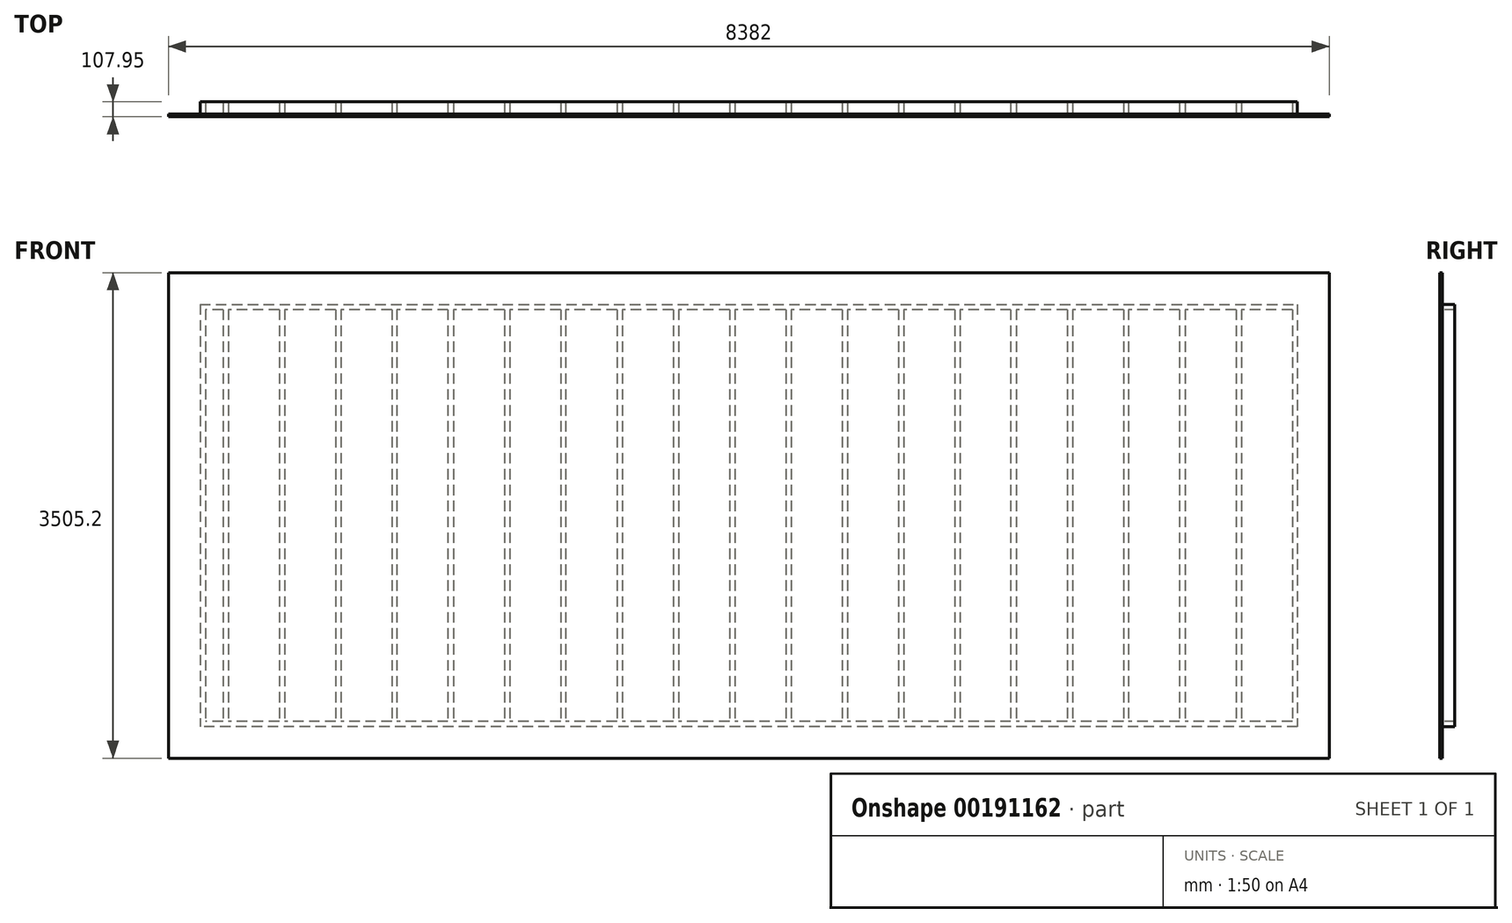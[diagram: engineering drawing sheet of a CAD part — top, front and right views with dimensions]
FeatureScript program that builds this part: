
annotation { "Feature Type Name" : "Feature", "Feature Type Description" : "" }
export const myFeature = defineFeature(function(context is Context, id is Id, definition is map)
    precondition{}
    {
        {
            var Q0;
            Q0=qCreatedBy(makeId("Top.planeOp"),FACE);
            var sketch = newSketch(context, id + "F0", { "sketchPlane" : qUnion([Q0])});
            skLineSegment(sketch, "E0.bottom", {"start": v(3962.4, -44.45) * mm, "end": v(-3962.4, -44.45) * mm});
            skLineSegment(sketch, "E0.top", {"start": v(3962.4, 44.45) * mm, "end": v(-3962.4, 44.45) * mm});
            skLineSegment(sketch, "E0.left", {"start": v(3962.4, -44.45) * mm, "end": v(3962.4, 44.45) * mm});
            skLineSegment(sketch, "E0.right", {"start": v(-3962.4, -44.45) * mm, "end": v(-3962.4, 44.45) * mm});
            skPoint(sketch, "E0.middle", {"position": v(0, 0) * mm});
            skSolve(sketch);
        }
        {
            var Q0;
            Q0 = qSketchRegion(id + "F0", true);
            extrude(context, id + "F1", {"entities" : qUnion([Q0]), "depth" : 38.1 * mm});
        }
        {
            var Q0;
            Q0=makeQuery(id+"F1.opExtrude","CAP_FACE",FACE,{"disambiguationData":[OSD([sQuery(id+"F0.wireOp",EDGE,"E0.bottom"),sQuery(id+"F0.wireOp",EDGE,"E0.top"),sQuery(id+"F0.wireOp",EDGE,"E0.left"),sQuery(id+"F0.wireOp",EDGE,"E0.right")])],"isStart":false});
            var sketch = newSketch(context, id + "F2", { "sketchPlane" : qUnion([Q0])});
            skLineSegment(sketch, "E1.bottom", {"start": v(3962.4, 44.45) * mm, "end": v(3924.3, 44.45) * mm});
            skLineSegment(sketch, "E1.top", {"start": v(3962.4, -44.45) * mm, "end": v(3924.3, -44.45) * mm});
            skLineSegment(sketch, "E1.left", {"start": v(3962.4, 44.45) * mm, "end": v(3962.4, -44.45) * mm});
            skLineSegment(sketch, "E1.right", {"start": v(3924.3, 44.45) * mm, "end": v(3924.3, -44.45) * mm});
            skLineSegment(sketch, "E2.bottom", {"start": v(3556, 44.45) * mm, "end": v(3517.9, 44.45) * mm});
            skLineSegment(sketch, "E2.top", {"start": v(3556, -44.45) * mm, "end": v(3517.9, -44.45) * mm});
            skLineSegment(sketch, "E2.left", {"start": v(3556, 44.45) * mm, "end": v(3556, -44.45) * mm});
            skLineSegment(sketch, "E2.right", {"start": v(3517.9, 44.45) * mm, "end": v(3517.9, -44.45) * mm});
            skLineSegment(sketch, "E3.bottom", {"start": v(3149.6, 44.45) * mm, "end": v(3111.5, 44.45) * mm});
            skLineSegment(sketch, "E3.top", {"start": v(3149.6, -44.45) * mm, "end": v(3111.5, -44.45) * mm});
            skLineSegment(sketch, "E3.left", {"start": v(3149.6, 44.45) * mm, "end": v(3149.6, -44.45) * mm});
            skLineSegment(sketch, "E3.right", {"start": v(3111.5, 44.45) * mm, "end": v(3111.5, -44.45) * mm});
            skLineSegment(sketch, "E4.bottom", {"start": v(2705.1, 44.45) * mm, "end": v(2743.2, 44.45) * mm});
            skLineSegment(sketch, "E4.top", {"start": v(2705.1, -44.45) * mm, "end": v(2743.2, -44.45) * mm});
            skLineSegment(sketch, "E4.left", {"start": v(2705.1, 44.45) * mm, "end": v(2705.1, -44.45) * mm});
            skLineSegment(sketch, "E4.right", {"start": v(2743.2, 44.45) * mm, "end": v(2743.2, -44.45) * mm});
            skLineSegment(sketch, "E5.bottom", {"start": v(2336.8, 44.45) * mm, "end": v(2298.7, 44.45) * mm});
            skLineSegment(sketch, "E5.top", {"start": v(2336.8, -44.45) * mm, "end": v(2298.7, -44.45) * mm});
            skLineSegment(sketch, "E5.left", {"start": v(2336.8, 44.45) * mm, "end": v(2336.8, -44.45) * mm});
            skLineSegment(sketch, "E5.right", {"start": v(2298.7, 44.45) * mm, "end": v(2298.7, -44.45) * mm});
            skLineSegment(sketch, "E6.bottom", {"start": v(1930.4, 44.45) * mm, "end": v(1892.3, 44.45) * mm});
            skLineSegment(sketch, "E6.top", {"start": v(1930.4, -44.45) * mm, "end": v(1892.3, -44.45) * mm});
            skLineSegment(sketch, "E6.left", {"start": v(1930.4, 44.45) * mm, "end": v(1930.4, -44.45) * mm});
            skLineSegment(sketch, "E6.right", {"start": v(1892.3, 44.45) * mm, "end": v(1892.3, -44.45) * mm});
            skLineSegment(sketch, "E7.bottom", {"start": v(1524, 44.45) * mm, "end": v(1485.9, 44.45) * mm});
            skLineSegment(sketch, "E7.top", {"start": v(1524, -44.45) * mm, "end": v(1485.9, -44.45) * mm});
            skLineSegment(sketch, "E7.left", {"start": v(1524, 44.45) * mm, "end": v(1524, -44.45) * mm});
            skLineSegment(sketch, "E7.right", {"start": v(1485.9, 44.45) * mm, "end": v(1485.9, -44.45) * mm});
            skLineSegment(sketch, "E8.bottom", {"start": v(1117.6, 44.45) * mm, "end": v(1079.5, 44.45) * mm});
            skLineSegment(sketch, "E8.top", {"start": v(1117.6, -44.45) * mm, "end": v(1079.5, -44.45) * mm});
            skLineSegment(sketch, "E8.left", {"start": v(1117.6, 44.45) * mm, "end": v(1117.6, -44.45) * mm});
            skLineSegment(sketch, "E8.right", {"start": v(1079.5, 44.45) * mm, "end": v(1079.5, -44.45) * mm});
            skLineSegment(sketch, "E9.bottom", {"start": v(711.2, 44.45) * mm, "end": v(673.1, 44.45) * mm});
            skLineSegment(sketch, "E9.top", {"start": v(711.2, -44.45) * mm, "end": v(673.1, -44.45) * mm});
            skLineSegment(sketch, "E9.left", {"start": v(711.2, 44.45) * mm, "end": v(711.2, -44.45) * mm});
            skLineSegment(sketch, "E9.right", {"start": v(673.1, 44.45) * mm, "end": v(673.1, -44.45) * mm});
            skLineSegment(sketch, "E10.bottom", {"start": v(304.8, 44.45) * mm, "end": v(266.7, 44.45) * mm});
            skLineSegment(sketch, "E10.top", {"start": v(304.8, -44.45) * mm, "end": v(266.7, -44.45) * mm});
            skLineSegment(sketch, "E10.left", {"start": v(304.8, 44.45) * mm, "end": v(304.8, -44.45) * mm});
            skLineSegment(sketch, "E10.right", {"start": v(266.7, 44.45) * mm, "end": v(266.7, -44.45) * mm});
            skLineSegment(sketch, "E11.bottom", {"start": v(-101.6, 44.45) * mm, "end": v(-139.7, 44.45) * mm});
            skLineSegment(sketch, "E11.top", {"start": v(-101.6, -44.45) * mm, "end": v(-139.7, -44.45) * mm});
            skLineSegment(sketch, "E11.left", {"start": v(-101.6, 44.45) * mm, "end": v(-101.6, -44.45) * mm});
            skLineSegment(sketch, "E11.right", {"start": v(-139.7, 44.45) * mm, "end": v(-139.7, -44.45) * mm});
            skLineSegment(sketch, "E12.bottom", {"start": v(-508, 44.45) * mm, "end": v(-546.1, 44.45) * mm});
            skLineSegment(sketch, "E12.top", {"start": v(-508, -44.45) * mm, "end": v(-546.1, -44.45) * mm});
            skLineSegment(sketch, "E12.left", {"start": v(-508, 44.45) * mm, "end": v(-508, -44.45) * mm});
            skLineSegment(sketch, "E12.right", {"start": v(-546.1, 44.45) * mm, "end": v(-546.1, -44.45) * mm});
            skLineSegment(sketch, "E13.bottom", {"start": v(-914.4, 44.45) * mm, "end": v(-952.5, 44.45) * mm});
            skLineSegment(sketch, "E13.top", {"start": v(-914.4, -44.45) * mm, "end": v(-952.5, -44.45) * mm});
            skLineSegment(sketch, "E13.left", {"start": v(-914.4, 44.45) * mm, "end": v(-914.4, -44.45) * mm});
            skLineSegment(sketch, "E13.right", {"start": v(-952.5, 44.45) * mm, "end": v(-952.5, -44.45) * mm});
            skLineSegment(sketch, "E14.bottom", {"start": v(-1320.8, 44.45) * mm, "end": v(-1358.9, 44.45) * mm});
            skLineSegment(sketch, "E14.top", {"start": v(-1320.8, -44.45) * mm, "end": v(-1358.9, -44.45) * mm});
            skLineSegment(sketch, "E14.left", {"start": v(-1320.8, 44.45) * mm, "end": v(-1320.8, -44.45) * mm});
            skLineSegment(sketch, "E14.right", {"start": v(-1358.9, 44.45) * mm, "end": v(-1358.9, -44.45) * mm});
            skLineSegment(sketch, "E15.bottom", {"start": v(-1727.2, 44.45) * mm, "end": v(-1765.3, 44.45) * mm});
            skLineSegment(sketch, "E15.top", {"start": v(-1727.2, -44.45) * mm, "end": v(-1765.3, -44.45) * mm});
            skLineSegment(sketch, "E15.left", {"start": v(-1727.2, 44.45) * mm, "end": v(-1727.2, -44.45) * mm});
            skLineSegment(sketch, "E15.right", {"start": v(-1765.3, 44.45) * mm, "end": v(-1765.3, -44.45) * mm});
            skLineSegment(sketch, "E16.bottom", {"start": v(-2133.6, 44.45) * mm, "end": v(-2171.7, 44.45) * mm});
            skLineSegment(sketch, "E16.top", {"start": v(-2133.6, -44.45) * mm, "end": v(-2171.7, -44.45) * mm});
            skLineSegment(sketch, "E16.left", {"start": v(-2133.6, 44.45) * mm, "end": v(-2133.6, -44.45) * mm});
            skLineSegment(sketch, "E16.right", {"start": v(-2171.7, 44.45) * mm, "end": v(-2171.7, -44.45) * mm});
            skLineSegment(sketch, "E17.bottom", {"start": v(-2540, 44.45) * mm, "end": v(-2578.1, 44.45) * mm});
            skLineSegment(sketch, "E17.top", {"start": v(-2540, -44.45) * mm, "end": v(-2578.1, -44.45) * mm});
            skLineSegment(sketch, "E17.left", {"start": v(-2540, 44.45) * mm, "end": v(-2540, -44.45) * mm});
            skLineSegment(sketch, "E17.right", {"start": v(-2578.1, 44.45) * mm, "end": v(-2578.1, -44.45) * mm});
            skLineSegment(sketch, "E18.bottom", {"start": v(-2946.4, 44.45) * mm, "end": v(-2984.5, 44.45) * mm});
            skLineSegment(sketch, "E18.top", {"start": v(-2946.4, -44.45) * mm, "end": v(-2984.5, -44.45) * mm});
            skLineSegment(sketch, "E18.left", {"start": v(-2946.4, 44.45) * mm, "end": v(-2946.4, -44.45) * mm});
            skLineSegment(sketch, "E18.right", {"start": v(-2984.5, 44.45) * mm, "end": v(-2984.5, -44.45) * mm});
            skLineSegment(sketch, "E19.bottom", {"start": v(-3962.4, 44.45) * mm, "end": v(-3924.3, 44.45) * mm});
            skLineSegment(sketch, "E19.top", {"start": v(-3962.4, -44.45) * mm, "end": v(-3924.3, -44.45) * mm});
            skLineSegment(sketch, "E19.left", {"start": v(-3962.4, 44.45) * mm, "end": v(-3962.4, -44.45) * mm});
            skLineSegment(sketch, "E19.right", {"start": v(-3924.3, 44.45) * mm, "end": v(-3924.3, -44.45) * mm});
            skLineSegment(sketch, "E20.bottom", {"start": v(-3390.9, 44.45) * mm, "end": v(-3352.8, 44.45) * mm});
            skLineSegment(sketch, "E20.top", {"start": v(-3390.9, -44.45) * mm, "end": v(-3352.8, -44.45) * mm});
            skLineSegment(sketch, "E20.left", {"start": v(-3390.9, 44.45) * mm, "end": v(-3390.9, -44.45) * mm});
            skLineSegment(sketch, "E20.right", {"start": v(-3352.8, 44.45) * mm, "end": v(-3352.8, -44.45) * mm});
            skLineSegment(sketch, "E21.bottom", {"start": v(-3797.3, 44.45) * mm, "end": v(-3759.2, 44.45) * mm});
            skLineSegment(sketch, "E21.top", {"start": v(-3797.3, -44.45) * mm, "end": v(-3759.2, -44.45) * mm});
            skLineSegment(sketch, "E21.left", {"start": v(-3797.3, 44.45) * mm, "end": v(-3797.3, -44.45) * mm});
            skLineSegment(sketch, "E21.right", {"start": v(-3759.2, 44.45) * mm, "end": v(-3759.2, -44.45) * mm});
            skSolve(sketch);
        }
        {
            var Q0;
            Q0 = qSketchRegion(id + "F2", true);
            extrude(context, id + "F3", {"entities" : qUnion([Q0]), "operationType" : NewBodyOperationType.ADD, "depth" : 2971.8 * mm});
        }
        {
            var Q0;
            Q0=makeQuery(id+"F3.boolean.opBoolean","MERGE",FACE,{"derivedFrom":[makeQuery(id+"F1.opExtrude","SWEPT_FACE",FACE,{"disambiguationData":[OSD([sQuery(id+"F0.wireOp",EDGE,"E0.bottom")])]}),makeQuery(id+"F3.opExtrude","SWEPT_FACE",FACE,{"disambiguationData":[OSD([sQuery(id+"F2.wireOp",EDGE,"E1.top")])]}),makeQuery(id+"F3.opExtrude","SWEPT_FACE",FACE,{"disambiguationData":[OSD([sQuery(id+"F2.wireOp",EDGE,"E2.top")])]}),makeQuery(id+"F3.opExtrude","SWEPT_FACE",FACE,{"disambiguationData":[OSD([sQuery(id+"F2.wireOp",EDGE,"E3.top")])]}),makeQuery(id+"F3.opExtrude","SWEPT_FACE",FACE,{"disambiguationData":[OSD([sQuery(id+"F2.wireOp",EDGE,"E4.top")])]}),makeQuery(id+"F3.opExtrude","SWEPT_FACE",FACE,{"disambiguationData":[OSD([sQuery(id+"F2.wireOp",EDGE,"E5.top")])]}),makeQuery(id+"F3.opExtrude","SWEPT_FACE",FACE,{"disambiguationData":[OSD([sQuery(id+"F2.wireOp",EDGE,"E6.top")])]}),makeQuery(id+"F3.opExtrude","SWEPT_FACE",FACE,{"disambiguationData":[OSD([sQuery(id+"F2.wireOp",EDGE,"E7.top")])]}),makeQuery(id+"F3.opExtrude","SWEPT_FACE",FACE,{"disambiguationData":[OSD([sQuery(id+"F2.wireOp",EDGE,"E8.top")])]}),makeQuery(id+"F3.opExtrude","SWEPT_FACE",FACE,{"disambiguationData":[OSD([sQuery(id+"F2.wireOp",EDGE,"E9.top")])]}),makeQuery(id+"F3.opExtrude","SWEPT_FACE",FACE,{"disambiguationData":[OSD([sQuery(id+"F2.wireOp",EDGE,"E10.top")])]}),makeQuery(id+"F3.opExtrude","SWEPT_FACE",FACE,{"disambiguationData":[OSD([sQuery(id+"F2.wireOp",EDGE,"E11.top")])]}),makeQuery(id+"F3.opExtrude","SWEPT_FACE",FACE,{"disambiguationData":[OSD([sQuery(id+"F2.wireOp",EDGE,"E12.top")])]}),makeQuery(id+"F3.opExtrude","SWEPT_FACE",FACE,{"disambiguationData":[OSD([sQuery(id+"F2.wireOp",EDGE,"E13.top")])]}),makeQuery(id+"F3.opExtrude","SWEPT_FACE",FACE,{"disambiguationData":[OSD([sQuery(id+"F2.wireOp",EDGE,"E14.top")])]}),makeQuery(id+"F3.opExtrude","SWEPT_FACE",FACE,{"disambiguationData":[OSD([sQuery(id+"F2.wireOp",EDGE,"E15.top")])]}),makeQuery(id+"F3.opExtrude","SWEPT_FACE",FACE,{"disambiguationData":[OSD([sQuery(id+"F2.wireOp",EDGE,"E16.top")])]}),makeQuery(id+"F3.opExtrude","SWEPT_FACE",FACE,{"disambiguationData":[OSD([sQuery(id+"F2.wireOp",EDGE,"E17.top")])]}),makeQuery(id+"F3.opExtrude","SWEPT_FACE",FACE,{"disambiguationData":[OSD([sQuery(id+"F2.wireOp",EDGE,"E18.top")])]}),makeQuery(id+"F3.opExtrude","SWEPT_FACE",FACE,{"disambiguationData":[OSD([sQuery(id+"F2.wireOp",EDGE,"E19.top")])]}),makeQuery(id+"F3.opExtrude","SWEPT_FACE",FACE,{"disambiguationData":[OSD([sQuery(id+"F2.wireOp",EDGE,"E20.top")])]}),makeQuery(id+"F3.opExtrude","SWEPT_FACE",FACE,{"disambiguationData":[OSD([sQuery(id+"F2.wireOp",EDGE,"E21.top")])]})]});
            var sketch = newSketch(context, id + "F4", { "sketchPlane" : qUnion([Q0])});
            skLineSegment(sketch, "E22.bottom", {"start": v(-3962.4, 3009.9) * mm, "end": v(3962.4, 3009.9) * mm});
            skLineSegment(sketch, "E22.top", {"start": v(-3962.4, 3048) * mm, "end": v(3962.4, 3048) * mm});
            skLineSegment(sketch, "E22.left", {"start": v(-3962.4, 3009.9) * mm, "end": v(-3962.4, 3048) * mm});
            skLineSegment(sketch, "E22.right", {"start": v(3962.4, 3009.9) * mm, "end": v(3962.4, 3048) * mm});
            skSolve(sketch);
        }
        {
            var Q0;
            Q0 = qSketchRegion(id + "F4", true);
            extrude(context, id + "F5", {"entities" : qUnion([Q0]), "operationType" : NewBodyOperationType.ADD, "oppositeDirection" : true, "depth" : 88.9 * mm});
        }
        {
            var Q0;
            Q0=makeQuery(id+"F5.boolean.opBoolean","MERGE",FACE,{"derivedFrom":[makeQuery(id+"F3.boolean.opBoolean","MERGE",FACE,{"derivedFrom":[makeQuery(id+"F1.opExtrude","SWEPT_FACE",FACE,{"disambiguationData":[OSD([sQuery(id+"F0.wireOp",EDGE,"E0.bottom")])]}),makeQuery(id+"F3.opExtrude","SWEPT_FACE",FACE,{"disambiguationData":[OSD([sQuery(id+"F2.wireOp",EDGE,"E1.top")])]}),makeQuery(id+"F3.opExtrude","SWEPT_FACE",FACE,{"disambiguationData":[OSD([sQuery(id+"F2.wireOp",EDGE,"E2.top")])]}),makeQuery(id+"F3.opExtrude","SWEPT_FACE",FACE,{"disambiguationData":[OSD([sQuery(id+"F2.wireOp",EDGE,"E3.top")])]}),makeQuery(id+"F3.opExtrude","SWEPT_FACE",FACE,{"disambiguationData":[OSD([sQuery(id+"F2.wireOp",EDGE,"E4.top")])]}),makeQuery(id+"F3.opExtrude","SWEPT_FACE",FACE,{"disambiguationData":[OSD([sQuery(id+"F2.wireOp",EDGE,"E5.top")])]}),makeQuery(id+"F3.opExtrude","SWEPT_FACE",FACE,{"disambiguationData":[OSD([sQuery(id+"F2.wireOp",EDGE,"E6.top")])]}),makeQuery(id+"F3.opExtrude","SWEPT_FACE",FACE,{"disambiguationData":[OSD([sQuery(id+"F2.wireOp",EDGE,"E7.top")])]}),makeQuery(id+"F3.opExtrude","SWEPT_FACE",FACE,{"disambiguationData":[OSD([sQuery(id+"F2.wireOp",EDGE,"E8.top")])]}),makeQuery(id+"F3.opExtrude","SWEPT_FACE",FACE,{"disambiguationData":[OSD([sQuery(id+"F2.wireOp",EDGE,"E9.top")])]}),makeQuery(id+"F3.opExtrude","SWEPT_FACE",FACE,{"disambiguationData":[OSD([sQuery(id+"F2.wireOp",EDGE,"E10.top")])]}),makeQuery(id+"F3.opExtrude","SWEPT_FACE",FACE,{"disambiguationData":[OSD([sQuery(id+"F2.wireOp",EDGE,"E11.top")])]}),makeQuery(id+"F3.opExtrude","SWEPT_FACE",FACE,{"disambiguationData":[OSD([sQuery(id+"F2.wireOp",EDGE,"E12.top")])]}),makeQuery(id+"F3.opExtrude","SWEPT_FACE",FACE,{"disambiguationData":[OSD([sQuery(id+"F2.wireOp",EDGE,"E13.top")])]}),makeQuery(id+"F3.opExtrude","SWEPT_FACE",FACE,{"disambiguationData":[OSD([sQuery(id+"F2.wireOp",EDGE,"E14.top")])]}),makeQuery(id+"F3.opExtrude","SWEPT_FACE",FACE,{"disambiguationData":[OSD([sQuery(id+"F2.wireOp",EDGE,"E15.top")])]}),makeQuery(id+"F3.opExtrude","SWEPT_FACE",FACE,{"disambiguationData":[OSD([sQuery(id+"F2.wireOp",EDGE,"E16.top")])]}),makeQuery(id+"F3.opExtrude","SWEPT_FACE",FACE,{"disambiguationData":[OSD([sQuery(id+"F2.wireOp",EDGE,"E17.top")])]}),makeQuery(id+"F3.opExtrude","SWEPT_FACE",FACE,{"disambiguationData":[OSD([sQuery(id+"F2.wireOp",EDGE,"E18.top")])]}),makeQuery(id+"F3.opExtrude","SWEPT_FACE",FACE,{"disambiguationData":[OSD([sQuery(id+"F2.wireOp",EDGE,"E19.top")])]}),makeQuery(id+"F3.opExtrude","SWEPT_FACE",FACE,{"disambiguationData":[OSD([sQuery(id+"F2.wireOp",EDGE,"E20.top")])]}),makeQuery(id+"F3.opExtrude","SWEPT_FACE",FACE,{"disambiguationData":[OSD([sQuery(id+"F2.wireOp",EDGE,"E21.top")])]})]}),makeQuery(id+"F5.opExtrude","CAP_FACE",FACE,{"disambiguationData":[OSD([sQuery(id+"F4.wireOp",EDGE,"E22.bottom"),sQuery(id+"F4.wireOp",EDGE,"E22.top"),sQuery(id+"F4.wireOp",EDGE,"E22.left"),sQuery(id+"F4.wireOp",EDGE,"E22.right")])],"isStart":true})]});
            var sketch = newSketch(context, id + "F6", { "sketchPlane" : qUnion([Q0])});
            skLineSegment(sketch, "E23.bottom", {"start": v(4191, 3276.6) * mm, "end": v(-4191, 3276.6) * mm});
            skLineSegment(sketch, "E23.top", {"start": v(4191, -228.6) * mm, "end": v(-4191, -228.6) * mm});
            skLineSegment(sketch, "E23.left", {"start": v(4191, 3276.6) * mm, "end": v(4191, -228.6) * mm});
            skLineSegment(sketch, "E23.right", {"start": v(-4191, 3276.6) * mm, "end": v(-4191, -228.6) * mm});
            skSolve(sketch);
        }
        {
            var Q0;
            Q0 = qSketchRegion(id + "F6", true);
            extrude(context, id + "F7", {"entities" : qUnion([Q0]), "operationType" : NewBodyOperationType.ADD, "depth" : 19.05 * mm});
        }
    });
